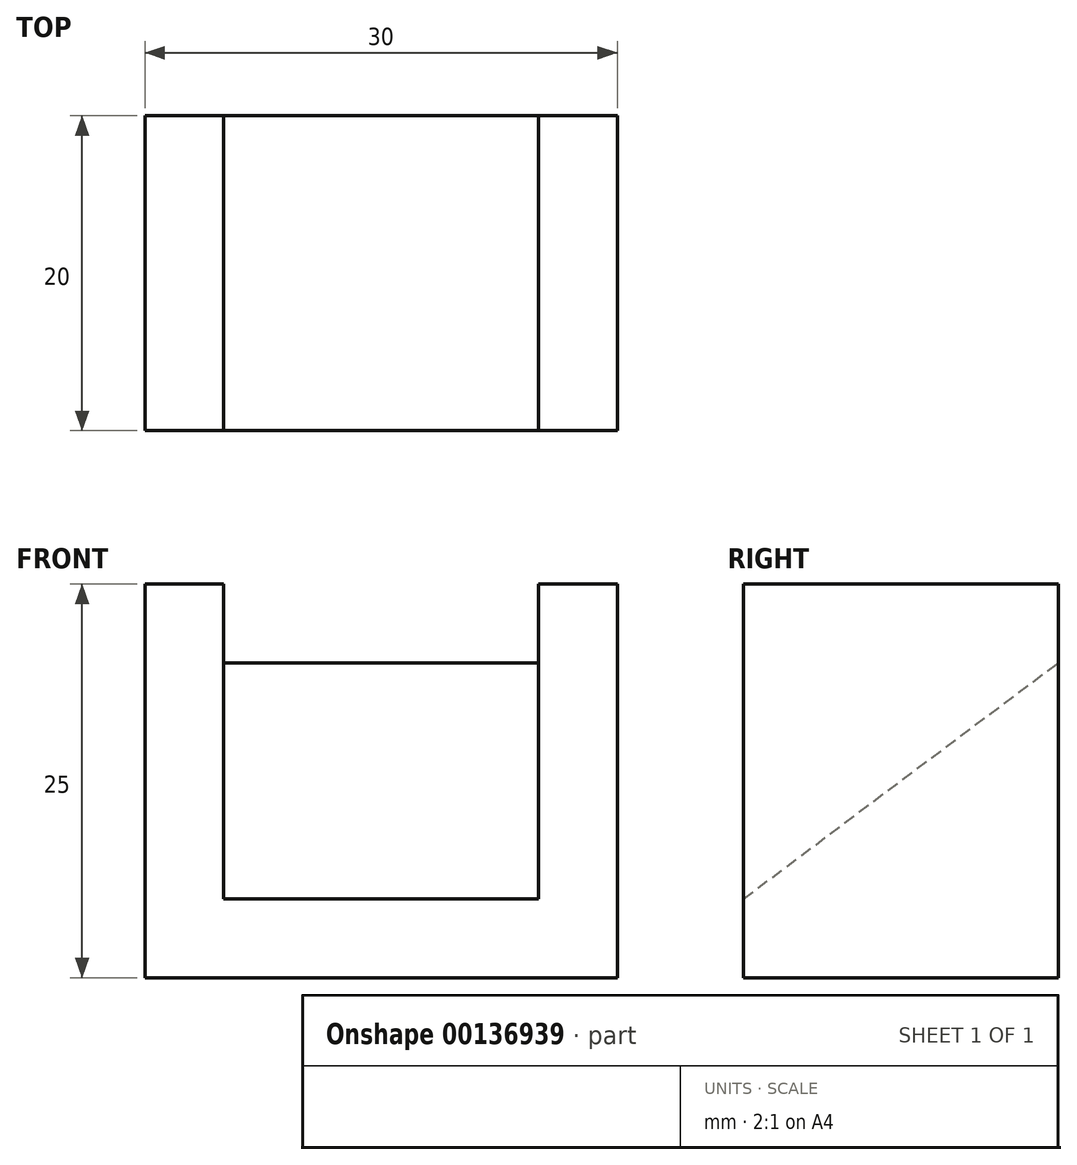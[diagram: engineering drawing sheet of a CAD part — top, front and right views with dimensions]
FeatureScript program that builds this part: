
annotation { "Feature Type Name" : "Feature", "Feature Type Description" : "" }
export const myFeature = defineFeature(function(context is Context, id is Id, definition is map)
    precondition{}
    {
        {
            var Q0;
            Q0=qCreatedBy(makeId("Right.planeOp"),FACE);
            var sketch = newSketch(context, id + "F0", { "sketchPlane" : qUnion([Q0])});
            skLineSegment(sketch, "E0.bottom", {"start": v(0, 0) * mm, "end": v(20, 0) * mm});
            skLineSegment(sketch, "E0.top", {"start": v(0, 20) * mm, "end": v(20, 20) * mm});
            skLineSegment(sketch, "E0.left", {"start": v(0, 0) * mm, "end": v(0, 20) * mm});
            skLineSegment(sketch, "E0.right", {"start": v(20, 0) * mm, "end": v(20, 20) * mm});
            skSolve(sketch);
        }
        {
            var Q0;
            Q0 = qSketchRegion(id + "F0", true);
            extrude(context, id + "F1", {"entities" : qUnion([Q0]), "oppositeDirection" : true, "depth" : 20 * mm});
        }
        {
            var Q0;
            Q0=makeQuery(id+"F1.opExtrude","CAP_FACE",FACE,{"disambiguationData":[OSD([sQuery(id+"F0.wireOp",EDGE,"E0.bottom"),sQuery(id+"F0.wireOp",EDGE,"E0.top"),sQuery(id+"F0.wireOp",EDGE,"E0.left"),sQuery(id+"F0.wireOp",EDGE,"E0.right")])],"isStart":true});
            var sketch = newSketch(context, id + "F2", { "sketchPlane" : qUnion([Q0])});
            skLineSegment(sketch, "E1", {"start": v(20, 0) * mm, "end": v(20, 25) * mm});
            skLineSegment(sketch, "E2", {"start": v(20, 25) * mm, "end": v(0, 25) * mm});
            skLineSegment(sketch, "E3", {"start": v(0, 25) * mm, "end": v(0, 0) * mm});
            skLineSegment(sketch, "E4", {"start": v(0, 0) * mm, "end": v(20, 0) * mm});
            skLineSegment(sketch, "E5", {"start": v(20, 20) * mm, "end": v(0, 20) * mm});
            skLineSegment(sketch, "E6", {"start": v(0, 20) * mm, "end": v(0, 5) * mm});
            skLineSegment(sketch, "E7", {"start": v(0, 5) * mm, "end": v(20, 20) * mm});
            skSolve(sketch);
        }
        {
            var Q0;
            Q0=makeQuery(id+"F1.opExtrude","CAP_FACE",FACE,{"disambiguationData":[OSD([sQuery(id+"F0.wireOp",EDGE,"E0.bottom"),sQuery(id+"F0.wireOp",EDGE,"E0.top"),sQuery(id+"F0.wireOp",EDGE,"E0.left"),sQuery(id+"F0.wireOp",EDGE,"E0.right")])],"isStart":false});
            var sketch = newSketch(context, id + "F3", { "sketchPlane" : qUnion([Q0])});
            skLineSegment(sketch, "E8", {"start": v(0, 0) * mm, "end": v(0, 25) * mm});
            skLineSegment(sketch, "E9", {"start": v(0, 25) * mm, "end": v(-20, 25) * mm});
            skLineSegment(sketch, "E10", {"start": v(-20, 25) * mm, "end": v(-20, 0) * mm});
            skLineSegment(sketch, "E11", {"start": v(-20, 0) * mm, "end": v(0, 0) * mm});
            skSolve(sketch);
        }
        {
            var Q0;
            {var subQ0=sQuery(id+"F3.wireOp",EDGE,"E11");Q0=makeQuery(id+"F3.imprint","IMPRINT",FACE,{"disambiguationData":[TD([[makeQuery(id+"F3.imprint","IMPRINT",EDGE,{"derivedFrom":subQ0}),-1.0]])]});}
            var Q1;
            {var subQ2=sQuery(id+"F3.wireOp",EDGE,"E9");Q1=makeQuery(id+"F3.imprint","IMPRINT",FACE,{"disambiguationData":[TD([[makeQuery(id+"F3.imprint","IMPRINT",EDGE,{"derivedFrom":subQ2}),1.0]])]});}
            extrude(context, id + "F4", {"entities" : qUnion([Q0, Q1]), "operationType" : NewBodyOperationType.ADD, "depth" : 5 * mm});
        }
        {
            var Q0;
            Q0=makeQuery(id+"F2.imprint","IMPRINT",FACE,{"disambiguationData":[TD([[makeQuery(id+"F2.imprint","IMPRINT",EDGE,{"derivedFrom":sQuery(id+"F2.wireOp",EDGE,"E5")}),-1.0]])]});
            extrude(context, id + "F5", {"entities" : qUnion([Q0]), "operationType" : NewBodyOperationType.REMOVE, "oppositeDirection" : true, "depth" : 20 * mm});
        }
        {
            var Q0;
            {var subQ2=sQuery(id+"F2.wireOp",EDGE,"E2");Q0=makeQuery(id+"F2.imprint","IMPRINT",FACE,{"disambiguationData":[TD([[makeQuery(id+"F2.imprint","IMPRINT",EDGE,{"derivedFrom":subQ2}),1.0]])]});}
            var Q1;
            Q1=makeQuery(id+"F2.imprint","IMPRINT",FACE,{"disambiguationData":[TD([[makeQuery(id+"F2.imprint","IMPRINT",EDGE,{"derivedFrom":sQuery(id+"F2.wireOp",EDGE,"E5")}),-1.0]])]});
            var Q2;
            {var subQ0=sQuery(id+"F2.wireOp",EDGE,"E4");Q2=makeQuery(id+"F2.imprint","IMPRINT",FACE,{"disambiguationData":[TD([[makeQuery(id+"F2.imprint","IMPRINT",EDGE,{"derivedFrom":subQ0}),1.0]])]});}
            extrude(context, id + "F6", {"entities" : qUnion([Q0, Q1, Q2]), "operationType" : NewBodyOperationType.ADD, "depth" : 5 * mm});
        }
    });
